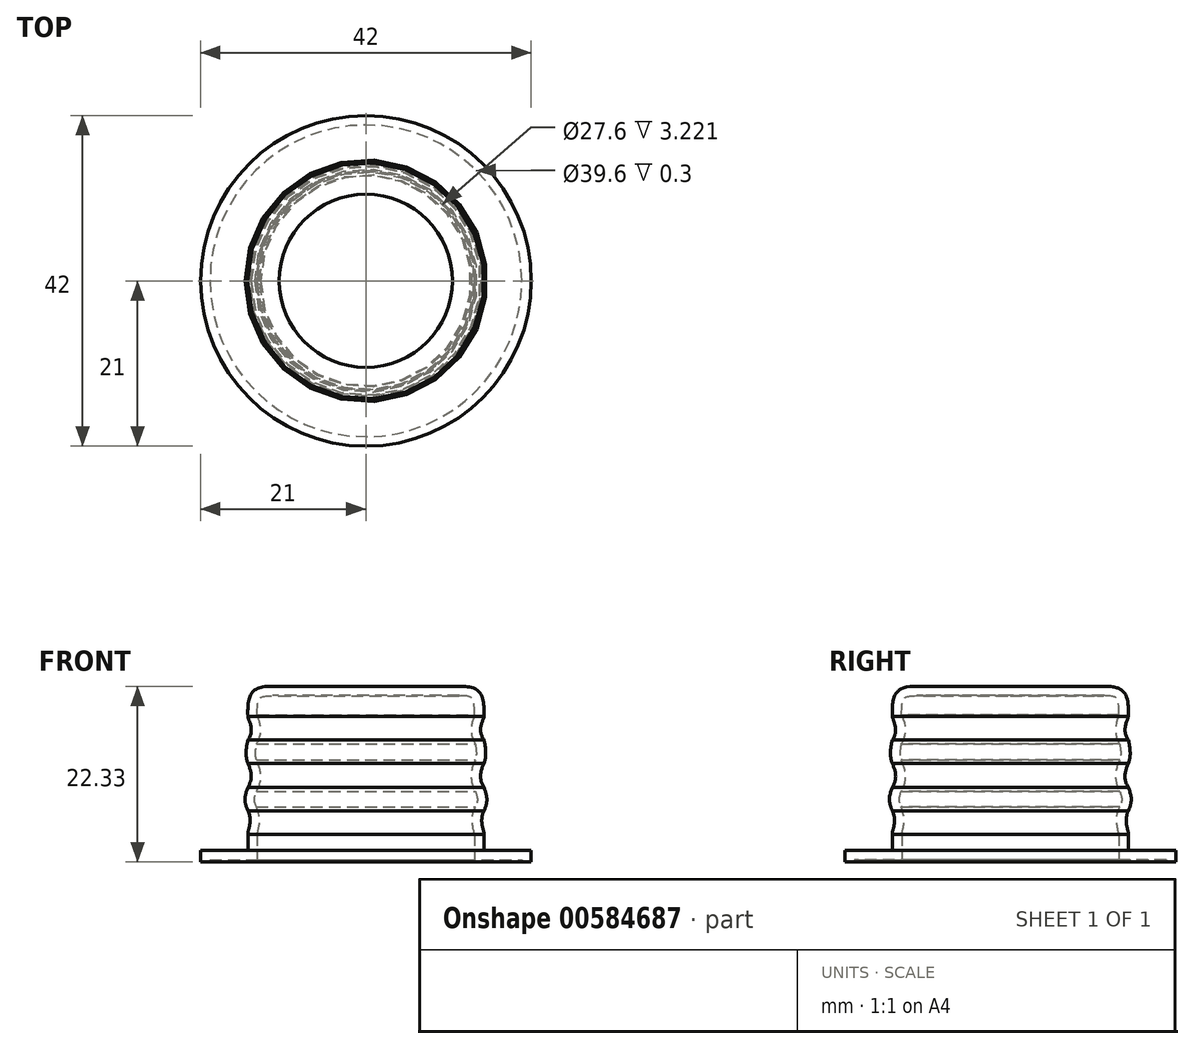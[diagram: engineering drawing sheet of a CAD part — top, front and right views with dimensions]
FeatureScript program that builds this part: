
annotation { "Feature Type Name" : "Feature", "Feature Type Description" : "" }
export const myFeature = defineFeature(function(context is Context, id is Id, definition is map)
    precondition{}
    {
        {
            var Q0;
            Q0=qCreatedBy(makeId("Front.planeOp"),FACE);
            var sketch = newSketch(context, id + "F0", { "sketchPlane" : qUnion([Q0])});
            skLineSegment(sketch, "E0.bottom", {"start": v(0, 0) * mm, "end": v(-21, 0) * mm});
            skLineSegment(sketch, "E0.top", {"start": v(0, 1.5) * mm, "end": v(-21, 1.5) * mm});
            skLineSegment(sketch, "E0.left", {"start": v(0, 0) * mm, "end": v(0, 1.5) * mm});
            skLineSegment(sketch, "E0.right", {"start": v(-21, 0) * mm, "end": v(-21, 1.5) * mm});
            skLineSegment(sketch, "E1.bottom", {"start": v(0, 1.5) * mm, "end": v(-15, 1.5) * mm});
            skLineSegment(sketch, "E1.top", {"start": v(0, 22.3) * mm, "end": v(-11, 22.3) * mm});
            skLineSegment(sketch, "E1.left", {"start": v(0, 1.5) * mm, "end": v(0, 22.5) * mm});
            skPoint(sketch, "E2", {"position": v(-15, 3.5) * mm});
            skPoint(sketch, "E3", {"position": v(-15, 6.5) * mm});
            skPoint(sketch, "E4", {"position": v(-15, 9.5) * mm});
            skPoint(sketch, "E5", {"position": v(-15, 12.5) * mm});
            skPoint(sketch, "E6", {"position": v(-15, 15.5) * mm});
            skPoint(sketch, "E7", {"position": v(-15, 18.5) * mm});
            skPoint(sketch, "E8.orphan", {"position": v(-15, 22.5) * mm});
            skLineSegment(sketch, "E9", {"start": v(-15, 1.5) * mm, "end": v(-15, 3.5) * mm});
            skFitSpline(sketch, "E10", {"points": [v(-15, 3.5) * mm, v(-15, 6.5) * mm], "startDerivative": vector(-0.1, 1.6) * mm, "endDerivative": vector(-1.97, 3.8) * mm});
            skFitSpline(sketch, "E11", {"points": [v(-15, 6.5) * mm, v(-15, 9.5) * mm], "startDerivative": vector(-1.44, 3.46) * mm, "endDerivative": vector(1.4, 3.94) * mm});
            skFitSpline(sketch, "E12", {"points": [v(-15, 9.5) * mm, v(-15, 12.5) * mm], "startDerivative": vector(1.75, 2.58) * mm, "endDerivative": vector(-1.75, 3.44) * mm});
            skFitSpline(sketch, "E13", {"points": [v(-15, 12.5) * mm, v(-15, 15.5) * mm], "startDerivative": vector(-1.07, 2.99) * mm, "endDerivative": vector(0.7, 3.26) * mm});
            skFitSpline(sketch, "E14", {"points": [v(-15, 15.5) * mm, v(-15, 18.5) * mm], "startDerivative": vector(2.86, 3.8) * mm, "endDerivative": vector(-0.11, 1.26) * mm});
            skFitSpline(sketch, "E15", {"points": [v(-15, 18.5) * mm, v(-11, 22.3) * mm], "startDerivative": vector(-0.23, 9.62) * mm, "endDerivative": vector(10.32, -0.6) * mm});
            skSolve(sketch);
        }
        {
            var Q0;
            {var subQ1=sQuery(id+"F0.wireOp",EDGE,"E1.top");Q0=makeQuery(id+"F0.imprint","IMPRINT",FACE,{"disambiguationData":[TD([[makeQuery(id+"F0.imprint","IMPRINT",EDGE,{"derivedFrom":subQ1}),1.0]])]});}
            var Q1;
            Q1=makeQuery(id+"F0.imprint","IMPRINT",FACE,{"disambiguationData":[TD([[makeQuery(id+"F0.imprint","IMPRINT",EDGE,{"derivedFrom":sQuery(id+"F0.wireOp",EDGE,"E0.bottom")}),-1.0]])]});
            var Q2;
            Q2=sQuery(id+"F0.wireOp",EDGE,"E1.left");
            revolve(context, id + "F1", {"surfaceOperationType" : NewSurfaceOperationType.NEW, "entities" : qUnion([Q0, Q1]), "axis" : qUnion([Q2]), "revolveType" : RevolveType.FULL});
        }
        {
            var Q0;
            Q0=makeQuery(id+"F1.opRevolve","SWEPT_FACE",FACE,{"disambiguationData":[OSD([sQuery(id+"F0.wireOp",EDGE,"E0.bottom")])]});
            shell(context, id + "F2", {"entities" : qUnion([Q0]), "thickness" : 1.2 * mm});
        }
    });
